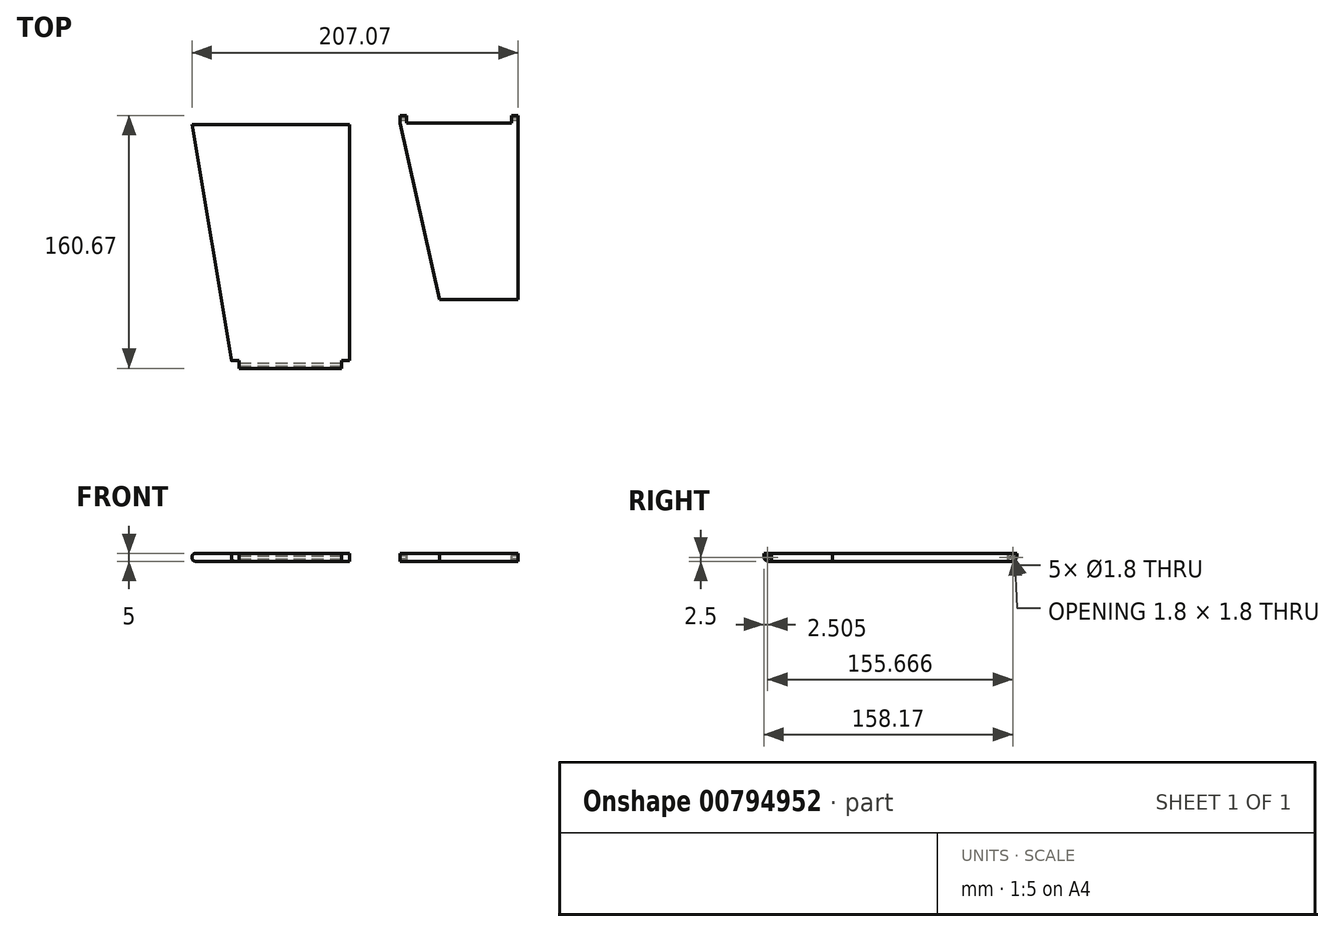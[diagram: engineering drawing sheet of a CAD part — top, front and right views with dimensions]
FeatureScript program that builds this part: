
annotation { "Feature Type Name" : "Feature", "Feature Type Description" : "" }
export const myFeature = defineFeature(function(context is Context, id is Id, definition is map)
    precondition{}
    {
        {
            var Q0;
            Q0=qCreatedBy(makeId("Top.planeOp"),FACE);
            var sketch = newSketch(context, id + "F0", { "sketchPlane" : qUnion([Q0])});
            skLineSegment(sketch, "E0.top", {"start": v(45.68, -36) * mm, "end": v(95.68, -36) * mm});
            skLineSegment(sketch, "E1", {"start": v(70.68, -36) * mm, "end": v(70.68, 114) * mm});
            skLineSegment(sketch, "E2", {"start": v(95.68, 76) * mm, "end": v(95.68, -36) * mm});
            skLineSegment(sketch, "E3", {"start": v(20.68, 76) * mm, "end": v(45.68, -36) * mm});
            skLineSegment(sketch, "E4", {"start": v(20.68, 76) * mm, "end": v(95.68, 76) * mm});
            skSolve(sketch);
        }
        {
            var Q0;
            Q0=qSketchRegion(id+"F0",true);
            extrude(context, id + "F1", {"entities" : qUnion([Q0]), "depth" : 5 * mm, "offsetDistance" : 25 * mm});
        }
        {
            var Q0;
            Q0=qCreatedBy(makeId("Top.planeOp"),FACE);
            var sketch = newSketch(context, id + "F2", { "sketchPlane" : qUnion([Q0])});
            skLineSegment(sketch, "E5.bottom", {"start": v(-111.4, 75.33) * mm, "end": v(-11.4, 75.33) * mm});
            skLineSegment(sketch, "E5.right", {"start": v(-11.4, 75.33) * mm, "end": v(-11.4, -74.67) * mm});
            skLineSegment(sketch, "E6", {"start": v(-111.4, 75.33) * mm, "end": v(-86.4, -74.67) * mm});
            skLineSegment(sketch, "E7", {"start": v(-36.4, -74.67) * mm, "end": v(-36.4, 75.33) * mm});
            skLineSegment(sketch, "E8", {"start": v(-86.4, -74.67) * mm, "end": v(-11.4, -74.67) * mm});
            skSolve(sketch);
        }
        {
            var Q0;
            Q0=qSketchRegion(id+"F2",true);
            extrude(context, id + "F3", {"entities" : qUnion([Q0]), "depth" : 5 * mm, "offsetDistance" : 25 * mm});
        }
        {
            var Q0;
            Q0=makeQuery(id+"F3.opExtrude","CAP_EDGE",EDGE,{"disambiguationData":[OSD([sQuery(id+"F2.wireOp",EDGE,"E6")])],"isStart":false});
            var Q1;
            Q1=makeQuery(id+"F3.opExtrude","CAP_EDGE",EDGE,{"disambiguationData":[OSD([sQuery(id+"F2.wireOp",EDGE,"E6")])],"isStart":true});
            fillet(context, id + "F4", {"entities" : qUnion([Q0, Q1]), "radius" : 2 * mm, "tangentPropagation" : true, "allowEdgeOverflow" : false});
        }
        {
            var Q0;
            Q0=makeQuery(id+"F1.opExtrude","SWEPT_FACE",FACE,{"disambiguationData":[OSD([sQuery(id+"F0.wireOp",EDGE,"E4")])]});
            var sketch = newSketch(context, id + "F5", { "sketchPlane" : qUnion([Q0])});
            skLineSegment(sketch, "E9.bottom", {"start": v(-95.68, 0) * mm, "end": v(-20.68, 0) * mm});
            skLineSegment(sketch, "E9.top", {"start": v(-95.68, 5) * mm, "end": v(-20.68, 5) * mm});
            skLineSegment(sketch, "E9.left", {"start": v(-95.68, 0) * mm, "end": v(-95.68, 5) * mm});
            skLineSegment(sketch, "E9.right", {"start": v(-20.68, 0) * mm, "end": v(-20.68, 5) * mm});
            skSolve(sketch);
        }
        {
            var Q0;
            Q0=qSketchRegion(id+"F5",true);
            extrude(context, id + "F6", {"entities" : qUnion([Q0]), "operationType" : NewBodyOperationType.ADD, "depth" : 5 * mm, "offsetDistance" : 25 * mm});
        }
        {
            var Q0;
            Q0=makeQuery(id+"F3.opExtrude","SWEPT_FACE",FACE,{"disambiguationData":[OSD([sQuery(id+"F2.wireOp",EDGE,"E8")])]});
            var sketch = newSketch(context, id + "F7", { "sketchPlane" : qUnion([Q0])});
            skLineSegment(sketch, "E10.bottom", {"start": v(-16.4, 0) * mm, "end": v(-81.4, 0) * mm});
            skLineSegment(sketch, "E10.top", {"start": v(-16.4, 5) * mm, "end": v(-81.4, 5) * mm});
            skLineSegment(sketch, "E10.left", {"start": v(-16.4, 0) * mm, "end": v(-16.4, 5) * mm});
            skLineSegment(sketch, "E10.right", {"start": v(-81.4, 0) * mm, "end": v(-81.4, 5) * mm});
            skSolve(sketch);
        }
        {
            var Q0;
            Q0=qSketchRegion(id+"F7",true);
            extrude(context, id + "F8", {"entities" : qUnion([Q0]), "operationType" : NewBodyOperationType.ADD, "depth" : 5 * mm, "offsetDistance" : 25 * mm});
        }
        {
            var Q0;
            Q0=makeQuery(id+"F6.opExtrude","CAP_FACE",FACE,{"disambiguationData":[OSD([sQuery(id+"F5.wireOp",EDGE,"E9.bottom"),sQuery(id+"F5.wireOp",EDGE,"E9.top"),sQuery(id+"F5.wireOp",EDGE,"E9.left"),sQuery(id+"F5.wireOp",EDGE,"E9.right")])],"isStart":false});
            var sketch = newSketch(context, id + "F9", { "sketchPlane" : qUnion([Q0])});
            skLineSegment(sketch, "E11.bottom", {"start": v(-24.83, -0.16) * mm, "end": v(-91.53, -0.16) * mm});
            skLineSegment(sketch, "E11.top", {"start": v(-24.83, 7.8) * mm, "end": v(-91.53, 7.8) * mm});
            skLineSegment(sketch, "E11.left", {"start": v(-24.83, -0.16) * mm, "end": v(-24.83, 7.8) * mm});
            skLineSegment(sketch, "E11.right", {"start": v(-91.53, -0.16) * mm, "end": v(-91.53, 7.8) * mm});
            skSolve(sketch);
        }
        {
            var Q0;
            Q0=qSketchRegion(id+"F9",true);
            extrude(context, id + "F10", {"entities" : qUnion([Q0]), "operationType" : NewBodyOperationType.REMOVE, "oppositeDirection" : true, "depth" : 5 * mm, "offsetDistance" : 25 * mm});
        }
        {
            var Q0;
            Q0=makeQuery(id+"F8.opExtrude","SWEPT_FACE",FACE,{"disambiguationData":[OSD([sQuery(id+"F7.wireOp",EDGE,"E10.left")])]});
            var sketch = newSketch(context, id + "F11", { "sketchPlane" : qUnion([Q0])});
            skCircle(sketch, "E12", {"center": v(-77.17, 2.5) * mm, "radius": 0.9 * mm});
            skPoint(sketch, "E12.centerSnap0", {"position": v(-77.17, 5) * mm});
            skPoint(sketch, "E12.centerSnap1", {"position": v(-79.67, 2.5) * mm});
            skSolve(sketch);
        }
        {
            var Q0;
            Q0=qSketchRegion(id+"F11",true);
            extrude(context, id + "F12", {"entities" : qUnion([Q0]), "operationType" : NewBodyOperationType.REMOVE, "oppositeDirection" : true, "depth" : 100 * mm, "offsetDistance" : 25 * mm});
        }
        {
            var Q0;
            Q0=makeQuery(id+"F6.opExtrude","SWEPT_FACE",FACE,{"disambiguationData":[OSD([sQuery(id+"F5.wireOp",EDGE,"E9.right")])]});
            var sketch = newSketch(context, id + "F13", { "sketchPlane" : qUnion([Q0])});
            skCircle(sketch, "E13", {"center": v(-78.5, 2.5) * mm, "radius": 0.9 * mm});
            skPoint(sketch, "E13.centerSnap0", {"position": v(-81, 2.5) * mm});
            skPoint(sketch, "E13.centerSnap1", {"position": v(-78.5, 0) * mm});
            skSolve(sketch);
        }
        {
            var Q0;
            Q0=qSketchRegion(id+"F13",true);
            extrude(context, id + "F14", {"entities" : qUnion([Q0]), "operationType" : NewBodyOperationType.REMOVE, "oppositeDirection" : true, "depth" : 125 * mm, "offsetDistance" : 25 * mm});
        }
        {
            var Q0;
            {var subQ0=sQuery(id+"F5.wireOp",EDGE,"E9.top");var subQ1=sQuery(id+"F5.wireOp",EDGE,"E9.right");Q0=makeQuery(id+"F10.boolean.opBoolean","SPLIT",EDGE,{"disambiguationData":[TD([makeQuery(id+"F6.opExtrude","SWEPT_FACE",FACE,{"disambiguationData":[OSD([subQ1])]})])],"derivedFrom":makeQuery(id+"F6.opExtrude","CAP_EDGE",EDGE,{"disambiguationData":[OSD([subQ0])],"isStart":false})});}
            var Q1;
            {var subQ0=sQuery(id+"F5.wireOp",EDGE,"E9.top");var subQ2=sQuery(id+"F0.wireOp",EDGE,"E2");Q1=makeQuery(id+"F10.boolean.opBoolean","SPLIT",EDGE,{"disambiguationData":[TD([makeQuery(id+"F1.opExtrude","SWEPT_FACE",FACE,{"disambiguationData":[OSD([subQ2])]})])],"derivedFrom":makeQuery(id+"F6.opExtrude","CAP_EDGE",EDGE,{"disambiguationData":[OSD([subQ0])],"isStart":false})});}
            var Q2;
            Q2=makeQuery(id+"F8.opExtrude","CAP_EDGE",EDGE,{"disambiguationData":[OSD([sQuery(id+"F7.wireOp",EDGE,"E10.top")])],"isStart":false});
            fillet(context, id + "F15", {"entities" : qUnion([Q0, Q1, Q2]), "radius" : 3 * mm, "tangentPropagation" : true, "allowEdgeOverflow" : false});
        }
        {
            var Q0;
            Q0=makeQuery(id+"F3.opExtrude","SWEPT_BODY",BODY,{"disambiguationData":[OSD([sQuery(id+"F2.wireOp",EDGE,"E5.bottom"),sQuery(id+"F2.wireOp",EDGE,"E5.right"),sQuery(id+"F2.wireOp",EDGE,"E6"),sQuery(id+"F2.wireOp",EDGE,"E8")])]});
            var Q1;
            Q1=makeQuery(id+"F1.opExtrude","SWEPT_BODY",BODY,{"disambiguationData":[OSD([sQuery(id+"F0.wireOp",EDGE,"E0.top"),sQuery(id+"F0.wireOp",EDGE,"E2"),sQuery(id+"F0.wireOp",EDGE,"E3"),sQuery(id+"F0.wireOp",EDGE,"E4")])]});
            var Q2;
            Q2=qCreatedBy(makeId("Top.planeOp"),FACE);
            mirror(context, id + "F16", {"entities" : qUnion([Q0, Q1]), "mirrorPlane" : qUnion([Q2])});
        }
        {
            var Q0;
            Q0=makeQuery(id+"F1.opExtrude","SWEPT_BODY",BODY,{"disambiguationData":[OSD([sQuery(id+"F0.wireOp",EDGE,"E0.top"),sQuery(id+"F0.wireOp",EDGE,"E2"),sQuery(id+"F0.wireOp",EDGE,"E3"),sQuery(id+"F0.wireOp",EDGE,"E4")])]});
            var Q1;
            Q1=qCreatedBy(makeId("Top.planeOp"),FACE);
            mirror(context, id + "F17", {"entities" : qUnion([Q0]), "mirrorPlane" : qUnion([Q1])});
        }
        {
            var Q0;
            Q0=makeQuery(id+"F3.opExtrude","SWEPT_BODY",BODY,{"disambiguationData":[OSD([sQuery(id+"F2.wireOp",EDGE,"E5.bottom"),sQuery(id+"F2.wireOp",EDGE,"E5.right"),sQuery(id+"F2.wireOp",EDGE,"E6"),sQuery(id+"F2.wireOp",EDGE,"E8")])]});
            var Q1;
            Q1=makeQuery(id+"F1.opExtrude","SWEPT_BODY",BODY,{"disambiguationData":[OSD([sQuery(id+"F0.wireOp",EDGE,"E0.top"),sQuery(id+"F0.wireOp",EDGE,"E2"),sQuery(id+"F0.wireOp",EDGE,"E3"),sQuery(id+"F0.wireOp",EDGE,"E4")])]});
            deleteBodies(context, id + "F18", {"entities" : qUnion([Q0, Q1])});
        }
    });
